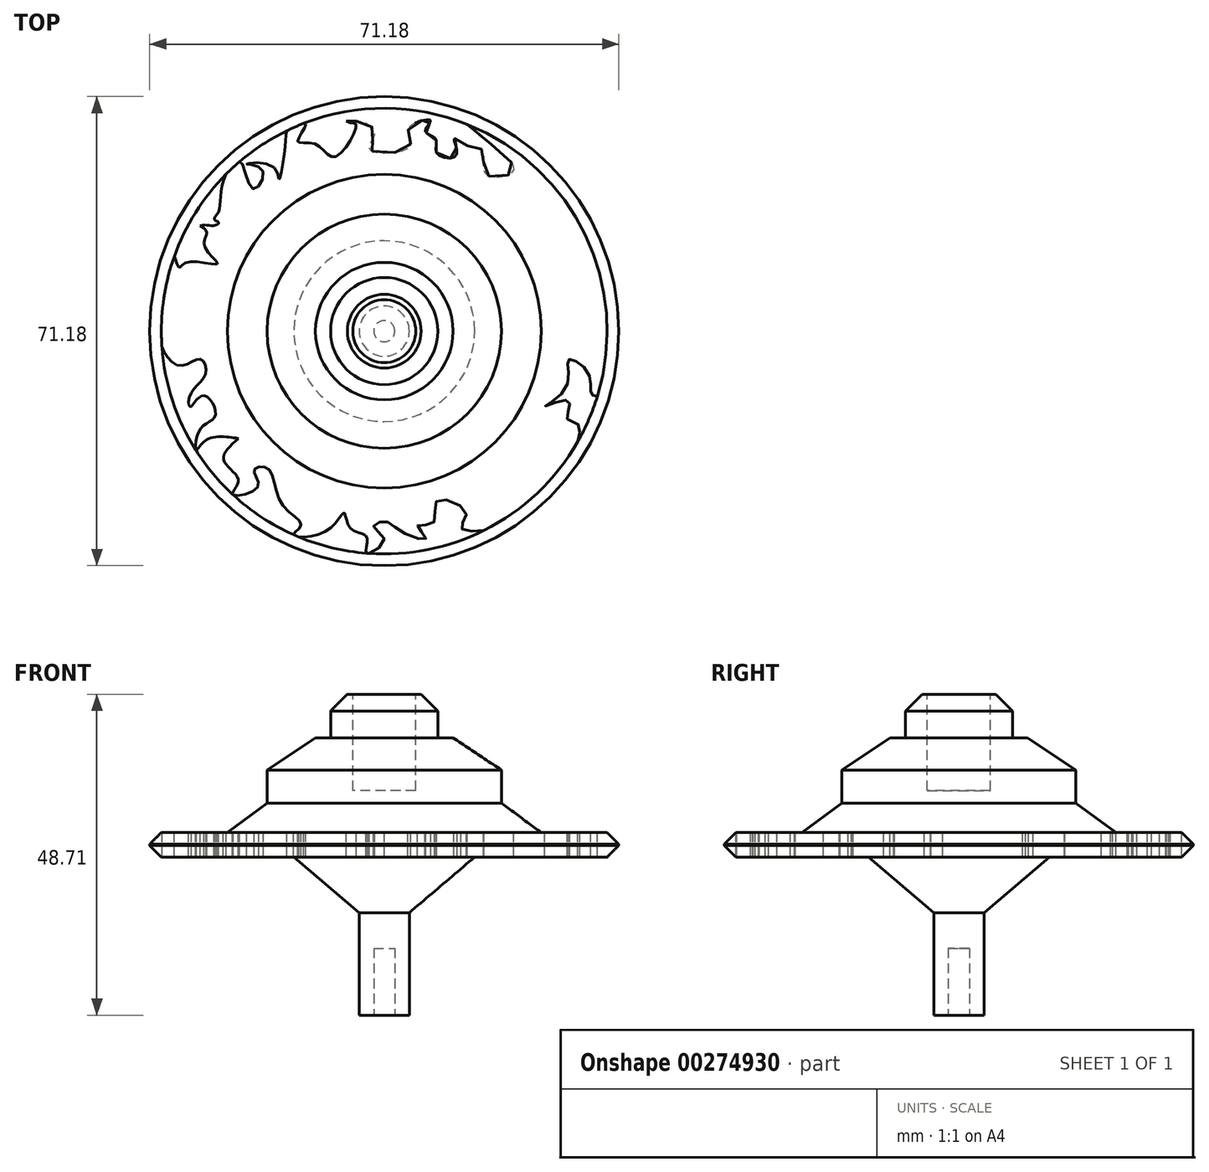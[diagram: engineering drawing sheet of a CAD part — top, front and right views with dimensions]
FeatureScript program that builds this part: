
annotation { "Feature Type Name" : "Feature", "Feature Type Description" : "" }
export const myFeature = defineFeature(function(context is Context, id is Id, definition is map)
    precondition{}
    {
        {
            var Q0;
            Q0=qCreatedBy(makeId("Right.planeOp"),FACE);
            var sketch = newSketch(context, id + "F0", { "sketchPlane" : qUnion([Q0])});
            skLineSegment(sketch, "E0", {"start": v(0, 0) * mm, "end": v(3.8, 0) * mm});
            skLineSegment(sketch, "E1", {"start": v(3.8, 0) * mm, "end": v(3.8, 15.55) * mm});
            skLineSegment(sketch, "E2", {"start": v(3.8, 15.55) * mm, "end": v(13.72, 23.99) * mm});
            skLineSegment(sketch, "E3", {"start": v(13.72, 23.99) * mm, "end": v(35.6, 23.99) * mm});
            skPoint(sketch, "E4.start.orphan", {"position": v(35.6, 26.13) * mm});
            skLineSegment(sketch, "E5", {"start": v(35.6, 23.99) * mm, "end": v(35.6, 27.72) * mm});
            skLineSegment(sketch, "E6", {"start": v(35.6, 27.72) * mm, "end": v(23.8, 27.72) * mm});
            skLineSegment(sketch, "E7", {"start": v(23.8, 27.72) * mm, "end": v(17.77, 32.18) * mm});
            skLineSegment(sketch, "E8", {"start": v(17.77, 32.18) * mm, "end": v(17.77, 37.21) * mm});
            skLineSegment(sketch, "E9", {"start": v(17.77, 37.21) * mm, "end": v(10.44, 42.1) * mm});
            skLineSegment(sketch, "E10", {"start": v(10.44, 42.1) * mm, "end": v(8.14, 42.1) * mm});
            skLineSegment(sketch, "E11", {"start": v(8.14, 42.1) * mm, "end": v(8.14, 48.71) * mm});
            skLineSegment(sketch, "E12", {"start": v(8.14, 48.71) * mm, "end": v(0, 48.71) * mm});
            skLineSegment(sketch, "E13", {"start": v(0, 48.71) * mm, "end": v(0, 0) * mm});
            skSolve(sketch);
        }
        {
            var Q0;
            Q0=makeQuery(id+"F0.imprint","IMPRINT",FACE,{"disambiguationData":[TD([[makeQuery(id+"F0.imprint","IMPRINT",EDGE,{"derivedFrom":sQuery(id+"F0.wireOp",EDGE,"E0")}),1.0]])]});
            var Q1;
            Q1=sQuery(id+"F0.wireOp",EDGE,"E13");
            revolve(context, id + "F1", {"entities" : qUnion([Q0]), "axis" : qUnion([Q1]), "revolveType" : RevolveType.FULL});
        }
        {
            var Q0;
            Q0=makeQuery(id+"F1.opRevolve","SWEPT_FACE",FACE,{"disambiguationData":[OSD([sQuery(id+"F0.wireOp",EDGE,"E12")])]});
            var sketch = newSketch(context, id + "F2", { "sketchPlane" : qUnion([Q0])});
            skCircle(sketch, "E14", {"center": v(0, 0) * mm, "radius": 4.78 * mm});
            skSolve(sketch);
        }
        {
            var Q0;
            Q0=makeQuery(id+"F2.imprint","IMPRINT",FACE,{"disambiguationData":[TD([[makeQuery(id+"F2.imprint","IMPRINT",EDGE,{"derivedFrom":sQuery(id+"F2.wireOp",EDGE,"E14")}),1.0]])]});
            extrude(context, id + "F3", {"entities" : qUnion([Q0]), "operationType" : NewBodyOperationType.ADD, "oppositeDirection" : true, "depth" : 14.6 * mm});
        }
        {
            var Q0;
            Q0=makeQuery(id+"F1.opRevolve","SWEPT_FACE",FACE,{"disambiguationData":[OSD([sQuery(id+"F0.wireOp",EDGE,"E12")])]});
            var sketch = newSketch(context, id + "F4", { "sketchPlane" : qUnion([Q0])});
            skCircle(sketch, "E15", {"center": v(0, 0) * mm, "radius": 4.78 * mm});
            skSolve(sketch);
        }
        {
            var Q0;
            Q0=makeQuery(id+"F4.imprint","IMPRINT",FACE,{"disambiguationData":[TD([[makeQuery(id+"F4.imprint","IMPRINT",EDGE,{"derivedFrom":sQuery(id+"F4.wireOp",EDGE,"E15")}),1.0]])]});
            extrude(context, id + "F5", {"entities" : qUnion([Q0]), "operationType" : NewBodyOperationType.REMOVE, "oppositeDirection" : true, "depth" : 14.6 * mm});
        }
        {
            var Q0;
            Q0=makeQuery(id+"F1.opRevolve","SWEPT_FACE",FACE,{"disambiguationData":[OSD([sQuery(id+"F0.wireOp",EDGE,"E0")])]});
            var sketch = newSketch(context, id + "F6", { "sketchPlane" : qUnion([Q0])});
            skCircle(sketch, "E16", {"center": v(0, 0) * mm, "radius": 1.6 * mm});
            skSolve(sketch);
        }
        {
            var Q0;
            Q0=makeQuery(id+"F6.imprint","IMPRINT",FACE,{"disambiguationData":[TD([[makeQuery(id+"F6.imprint","IMPRINT",EDGE,{"derivedFrom":sQuery(id+"F6.wireOp",EDGE,"E16")}),1.0]])]});
            extrude(context, id + "F7", {"entities" : qUnion([Q0]), "operationType" : NewBodyOperationType.REMOVE, "oppositeDirection" : true, "depth" : 10.16 * mm});
        }
        {
            var Q0;
            Q0=makeQuery(id+"F1.opRevolve","SWEPT_EDGE",EDGE,{"disambiguationData":[OSD([sQuery(id+"F0.wireOp",EDGE,"E3"),sQuery(id+"F0.wireOp",EDGE,"E5")])]});
            chamfer(context, id + "F8", {"entities" : qUnion([Q0]), "width" : 1.78 * mm, "tangentPropagation" : true});
        }
        {
            var Q0;
            Q0=makeQuery(id+"F1.opRevolve","SWEPT_EDGE",EDGE,{"disambiguationData":[OSD([sQuery(id+"F0.wireOp",EDGE,"E5"),sQuery(id+"F0.wireOp",EDGE,"E6")])]});
            chamfer(context, id + "F9", {"entities" : qUnion([Q0]), "width" : 1.78 * mm, "tangentPropagation" : true});
        }
        {
            var Q0;
            Q0=makeQuery(id+"F1.opRevolve","SWEPT_EDGE",EDGE,{"disambiguationData":[OSD([sQuery(id+"F0.wireOp",EDGE,"E11"),sQuery(id+"F0.wireOp",EDGE,"E12")])]});
            chamfer(context, id + "F10", {"entities" : qUnion([Q0]), "width" : 2.54 * mm, "tangentPropagation" : true});
        }
        {
            var Q0;
            Q0=makeQuery(id+"F1.opRevolve","SWEPT_FACE",FACE,{"disambiguationData":[OSD([sQuery(id+"F0.wireOp",EDGE,"E6")])]});
            var sketch = newSketch(context, id + "F11", { "sketchPlane" : qUnion([Q0])});
            skFitSpline(sketch, "E17", {"points": [v(-23.97, 23.85) * mm, v(-25.17, 17.97) * mm, v(-25.8, 16.99) * mm, v(-25.12, 16.46) * mm, v(-26.08, 16) * mm, v(-27.91, 16) * mm], "startDerivative": vector(-11.08, -21.67) * mm, "endDerivative": vector(-15.63, -4.02) * mm});
            skFitSpline(sketch, "E18", {"points": [v(-27.91, 16) * mm, v(-26.92, 14.93) * mm, v(-27.3, 12.95) * mm, v(-25.32, 10.2) * mm, v(-29.97, 10.44) * mm, v(-31.19, 9.67) * mm, v(-31.9, 11.23) * mm, v(-32.02, 7.92) * mm, v(-29.2, 6.93) * mm, v(-27.15, 5.26) * mm, v(-27.15, 5.18) * mm], "startDerivative": vector(17.74, -11.58) * mm, "endDerivative": vector(-1.26, -2.8) * mm});
            skFitSpline(sketch, "E19", {"points": [v(-27.14, 5.2) * mm, v(-29.74, 5.2) * mm, v(-31.87, 4.42) * mm, v(-32.4, 2.75) * mm, v(-32.48, 2.82) * mm], "startDerivative": vector(-7.58, 0.16) * mm, "endDerivative": vector(-1.14, 1.98) * mm});
            skFitSpline(sketch, "E20", {"points": [v(-32.4, 2.75) * mm, v(-30.5, 3.96) * mm, v(-28.83, 1.45) * mm, v(-30.2, -2.43) * mm, v(-31.87, -2.74) * mm, v(-33.75, -1.98) * mm, v(-31.34, -5.17) * mm, v(-27.91, -4.26) * mm, v(-27.14, -6.54) * mm, v(-29.28, -9.36) * mm, v(-29.51, -11.42) * mm, v(-29.28, -11.42) * mm, v(-29.36, -11.42) * mm], "startDerivative": vector(21.84, 23.02) * mm, "endDerivative": vector(-7.5, -0.67) * mm});
            skFitSpline(sketch, "E21", {"points": [v(-29.28, -11.42) * mm, v(-27.14, -9.82) * mm, v(-25.63, -12.79) * mm, v(-27.91, -14.84) * mm, v(-28.6, -18.04) * mm, v(-28.52, -18.17) * mm], "startDerivative": vector(9.4, 12.54) * mm, "endDerivative": vector(1.65, -1.16) * mm});
            skFitSpline(sketch, "E22", {"points": [v(-28.52, -18.17) * mm, v(-25.98, -16.13) * mm, v(-22.13, -16.3) * mm, v(-22.3, -16.3) * mm], "startDerivative": vector(4.17, 6.12) * mm, "endDerivative": vector(-2.75, 0.16) * mm});
            skFitSpline(sketch, "E23", {"points": [v(-22.13, -16.3) * mm, v(-24.35, -19.63) * mm, v(-22.13, -22.7) * mm, v(-22.96, -24.82) * mm, v(-19.14, -23.56) * mm, v(-19.74, -21.09) * mm, v(-17.69, -20.83) * mm, v(-15.55, -26.21) * mm, v(-12.64, -29.46) * mm, v(-13.76, -30.89) * mm, v(-8.8, -30.32) * mm, v(-6.06, -27.58) * mm, v(-5.12, -29.97) * mm, v(-2.64, -31.26) * mm, v(-2.67, -33.7) * mm, v(0, -31.6) * mm, v(-1.62, -29.72) * mm, v(0, -28.86) * mm, v(2.4, -30.32) * mm, v(6.33, -31.43) * mm, v(5.05, -29.55) * mm, v(7.44, -29.12) * mm, v(7.95, -25.79) * mm, v(12.4, -27.5) * mm, v(11.63, -29.8) * mm, v(15.12, -30.24) * mm], "startDerivative": vector(-85.14, -75.43) * mm, "endDerivative": vector(86.29, 18.11) * mm});
            skFitSpline(sketch, "E24", {"points": [v(15.12, -30.24) * mm, v(15.48, -27.5) * mm, v(15.12, -23.72) * mm, v(16.5, -20.57) * mm, v(19.75, -19.97) * mm, v(20.18, -22.45) * mm, v(22.14, -22.97) * mm, v(24.36, -22.03) * mm, v(24.2, -21.94) * mm], "startDerivative": vector(-21.05, 10.96) * mm, "endDerivative": vector(-7.35, 1.53) * mm});
            skFitSpline(sketch, "E25", {"points": [v(24.2, -21.94) * mm, v(21.8, -21.94) * mm, v(22.74, -19.12) * mm, v(22.06, -15.53) * mm, v(26.42, -14.85) * mm, v(26.5, -16.73) * mm, v(28.55, -16.3) * mm, v(29.07, -17.27) * mm, v(29.5, -14.25) * mm, v(27.78, -13.3) * mm, v(27.95, -10.57) * mm, v(24.36, -11.43) * mm, v(27.7, -8.35) * mm, v(27.95, -4.33) * mm, v(31.03, -6.47) * mm, v(31.37, -9.46) * mm, v(32.33, -9.9) * mm], "startDerivative": vector(-58.41, -10.28) * mm, "endDerivative": vector(31.05, -4.48) * mm});
            skFitSpline(sketch, "E26", {"points": [v(32.33, -9.9) * mm, v(33.56, -4.13) * mm, v(31.53, -1.38) * mm, v(32.33, 4.33) * mm, v(28.71, 3.8) * mm, v(28.71, 7.07) * mm, v(31.22, 10.2) * mm, v(30.84, 11.1) * mm, v(28.18, 14.82) * mm], "startDerivative": vector(15.65, 38.72) * mm, "endDerivative": vector(-0.36, 6.76) * mm});
            skFitSpline(sketch, "E27", {"points": [v(28.22, 14.83) * mm, v(26.32, 17.04) * mm, v(21.9, 16.68) * mm, v(23.6, 21.45) * mm, v(23.32, 24.48) * mm, v(16.32, 29.61) * mm, v(12.59, 31.38) * mm], "startDerivative": vector(-11.62, 18.06) * mm, "endDerivative": vector(4.68, -2.6) * mm});
            skFitSpline(sketch, "E28", {"points": [v(12.59, 31.38) * mm, v(19.61, 24.41) * mm, v(15.5, 23.75) * mm, v(15.02, 27.31) * mm, v(12.59, 28.16) * mm, v(10.6, 29.2) * mm, v(10.9, 26.65) * mm, v(7.96, 27) * mm, v(7.83, 29.13) * mm, v(6.2, 30.46) * mm, v(7.04, 31.97) * mm, v(3.72, 30.82) * mm, v(3.84, 27.98) * mm, v(-2.15, 27.56) * mm, v(-1.42, 30.21) * mm, v(-4.32, 31.9) * mm, v(-5.77, 31.85) * mm, v(-5.95, 31.9) * mm], "startDerivative": vector(69.22, -69.47) * mm, "endDerivative": vector(-9.87, 5.49) * mm});
            skFitSpline(sketch, "E29", {"points": [v(-5.77, 31.85) * mm, v(-4.26, 31.38) * mm, v(-7.46, 26.47) * mm, v(-10.42, 28.4) * mm, v(-13.14, 28.82) * mm, v(-11.93, 31.38) * mm, v(-14.49, 30.7) * mm, v(-14.95, 28.87) * mm, v(-15.92, 23.02) * mm, v(-16.83, 24.96) * mm, v(-20.88, 25.38) * mm, v(-18.46, 24.41) * mm, v(-19.97, 21.63) * mm, v(-21.94, 25.73) * mm, v(-23.97, 23.85) * mm], "startDerivative": vector(36.28, -28.23) * mm, "endDerivative": vector(-39.1, 74.42) * mm});
            skCircle(sketch, "E30", {"center": v(0, 0) * mm, "radius": 26.17 * mm});
            skSolve(sketch);
        }
        {
            var Q0;
            {var subQ0=sQuery(id+"F11.wireOp",EDGE,"E29");var subQ1=sQuery(id+"F0.wireOp",EDGE,"E6");var subQ2=makeQuery(id+"F9.opChamfer","BLEND_EDGE",EDGE,{"blendedFrom":[makeQuery(id+"F1.opRevolve","SWEPT_EDGE",EDGE,{"disambiguationData":[OSD([sQuery(id+"F0.wireOp",EDGE,"E5"),subQ1])]}),makeQuery(id+"F1.opRevolve","SWEPT_FACE",FACE,{"disambiguationData":[OSD([subQ1])]})],"blendedInto":[makeQuery(id+"F1.opRevolve","SWEPT_FACE",FACE,{"disambiguationData":[OSD([subQ1])]})]});var subQ3=makeQuery(id+"F11.imprint","INTERSECT",VERTEX,{"disambiguationData":[OD(1.0)],"derivedFrom":[subQ2,subQ0]});Q0=makeQuery(id+"F11.imprint","IMPRINT",FACE,{"disambiguationData":[TD([[makeQuery(id+"F11.imprint","IMPRINT",EDGE,{"disambiguationData":[TD([[subQ3,-1.0]])],"derivedFrom":subQ0}),-1.0]])]});}
            var Q1;
            {var subQ0=sQuery(id+"F11.wireOp",EDGE,"E17");Q1=makeQuery(id+"F11.imprint","IMPRINT",FACE,{"disambiguationData":[TD([[makeQuery(id+"F11.imprint","IMPRINT",EDGE,{"derivedFrom":subQ0}),-1.0]])]});}
            var Q2;
            {var subQ0=sQuery(id+"F11.wireOp",EDGE,"E21");var subQ1=sQuery(id+"F11.wireOp",EDGE,"E20");var subQ2=makeQuery(id+"F11.imprint","INTERSECT",VERTEX,{"derivedFrom":[subQ1,subQ0]});Q2=makeQuery(id+"F11.imprint","IMPRINT",FACE,{"disambiguationData":[TD([[makeQuery(id+"F11.imprint","IMPRINT",EDGE,{"disambiguationData":[TD([[subQ2,1.0]])],"derivedFrom":subQ1}),-1.0]])]});}
            var Q3;
            {var subQ0=sQuery(id+"F11.wireOp",EDGE,"E23");var subQ1=sQuery(id+"F0.wireOp",EDGE,"E6");var subQ2=makeQuery(id+"F9.opChamfer","BLEND_EDGE",EDGE,{"blendedFrom":[makeQuery(id+"F1.opRevolve","SWEPT_EDGE",EDGE,{"disambiguationData":[OSD([sQuery(id+"F0.wireOp",EDGE,"E5"),subQ1])]}),makeQuery(id+"F1.opRevolve","SWEPT_FACE",FACE,{"disambiguationData":[OSD([subQ1])]})],"blendedInto":[makeQuery(id+"F1.opRevolve","SWEPT_FACE",FACE,{"disambiguationData":[OSD([subQ1])]})]});var subQ3=makeQuery(id+"F11.imprint","INTERSECT",VERTEX,{"disambiguationData":[OD(1.0)],"derivedFrom":[subQ2,subQ0]});Q3=makeQuery(id+"F11.imprint","IMPRINT",FACE,{"disambiguationData":[TD([[makeQuery(id+"F11.imprint","IMPRINT",EDGE,{"disambiguationData":[TD([[subQ3,-1.0]])],"derivedFrom":subQ0}),-1.0]])]});}
            var Q4;
            {var subQ0=sQuery(id+"F11.wireOp",EDGE,"E23");var subQ1=sQuery(id+"F0.wireOp",EDGE,"E6");var subQ2=makeQuery(id+"F9.opChamfer","BLEND_EDGE",EDGE,{"blendedFrom":[makeQuery(id+"F1.opRevolve","SWEPT_EDGE",EDGE,{"disambiguationData":[OSD([sQuery(id+"F0.wireOp",EDGE,"E5"),subQ1])]}),makeQuery(id+"F1.opRevolve","SWEPT_FACE",FACE,{"disambiguationData":[OSD([subQ1])]})],"blendedInto":[makeQuery(id+"F1.opRevolve","SWEPT_FACE",FACE,{"disambiguationData":[OSD([subQ1])]})]});var subQ4=makeQuery(id+"F11.imprint","INTERSECT",VERTEX,{"disambiguationData":[OD(5.0)],"derivedFrom":[subQ2,subQ0]});Q4=makeQuery(id+"F11.imprint","IMPRINT",FACE,{"disambiguationData":[TD([[makeQuery(id+"F11.imprint","IMPRINT",EDGE,{"disambiguationData":[TD([[subQ4,-1.0]])],"derivedFrom":subQ0}),-1.0]])]});}
            var Q5;
            {var subQ0=sQuery(id+"F11.wireOp",EDGE,"E25");var subQ1=sQuery(id+"F0.wireOp",EDGE,"E6");var subQ2=makeQuery(id+"F9.opChamfer","BLEND_EDGE",EDGE,{"blendedFrom":[makeQuery(id+"F1.opRevolve","SWEPT_EDGE",EDGE,{"disambiguationData":[OSD([sQuery(id+"F0.wireOp",EDGE,"E5"),subQ1])]}),makeQuery(id+"F1.opRevolve","SWEPT_FACE",FACE,{"disambiguationData":[OSD([subQ1])]})],"blendedInto":[makeQuery(id+"F1.opRevolve","SWEPT_FACE",FACE,{"disambiguationData":[OSD([subQ1])]})]});var subQ4=makeQuery(id+"F11.imprint","INTERSECT",VERTEX,{"disambiguationData":[OD(1.0)],"derivedFrom":[subQ2,subQ0]});Q5=makeQuery(id+"F11.imprint","IMPRINT",FACE,{"disambiguationData":[TD([[makeQuery(id+"F11.imprint","IMPRINT",EDGE,{"disambiguationData":[TD([[subQ4,-1.0]])],"derivedFrom":subQ0}),-1.0]])]});}
            var Q6;
            {var subQ0=sQuery(id+"F11.wireOp",EDGE,"E28");var subQ4=sQuery(id+"F11.wireOp",EDGE,"E29");var subQ5=makeQuery(id+"F11.imprint","INTERSECT",VERTEX,{"derivedFrom":[subQ0,subQ4]});Q6=makeQuery(id+"F11.imprint","IMPRINT",FACE,{"disambiguationData":[TD([[makeQuery(id+"F11.imprint","IMPRINT",EDGE,{"disambiguationData":[TD([[subQ5,-1.0]])],"derivedFrom":subQ4}),-1.0]])]});}
            var Q7;
            {var subQ0=sQuery(id+"F11.wireOp",EDGE,"E23");var subQ1=sQuery(id+"F0.wireOp",EDGE,"E6");var subQ2=makeQuery(id+"F9.opChamfer","BLEND_EDGE",EDGE,{"blendedFrom":[makeQuery(id+"F1.opRevolve","SWEPT_EDGE",EDGE,{"disambiguationData":[OSD([sQuery(id+"F0.wireOp",EDGE,"E5"),subQ1])]}),makeQuery(id+"F1.opRevolve","SWEPT_FACE",FACE,{"disambiguationData":[OSD([subQ1])]})],"blendedInto":[makeQuery(id+"F1.opRevolve","SWEPT_FACE",FACE,{"disambiguationData":[OSD([subQ1])]})]});var subQ3=makeQuery(id+"F11.imprint","INTERSECT",VERTEX,{"disambiguationData":[OD(3.0)],"derivedFrom":[subQ2,subQ0]});Q7=makeQuery(id+"F11.imprint","IMPRINT",FACE,{"disambiguationData":[TD([[makeQuery(id+"F11.imprint","IMPRINT",EDGE,{"disambiguationData":[TD([[subQ3,-1.0]])],"derivedFrom":subQ0}),-1.0]])]});}
            var Q8;
            {var subQ0=sQuery(id+"F11.wireOp",EDGE,"E22");var subQ4=sQuery(id+"F11.wireOp",EDGE,"E23");var subQ5=makeQuery(id+"F11.imprint","INTERSECT",VERTEX,{"disambiguationData":[OD(0.0)],"derivedFrom":[subQ0,subQ4]});Q8=makeQuery(id+"F11.imprint","IMPRINT",FACE,{"disambiguationData":[TD([[makeQuery(id+"F11.imprint","IMPRINT",EDGE,{"disambiguationData":[TD([[subQ5,-1.0]])],"derivedFrom":subQ4}),-1.0]])]});}
            extrude(context, id + "F12", {"entities" : qUnion([Q0, Q1, Q2, Q3, Q4, Q5, Q6, Q7, Q8]), "operationType" : NewBodyOperationType.REMOVE, "oppositeDirection" : true, "depth" : 26.92 * mm});
        }
    });
